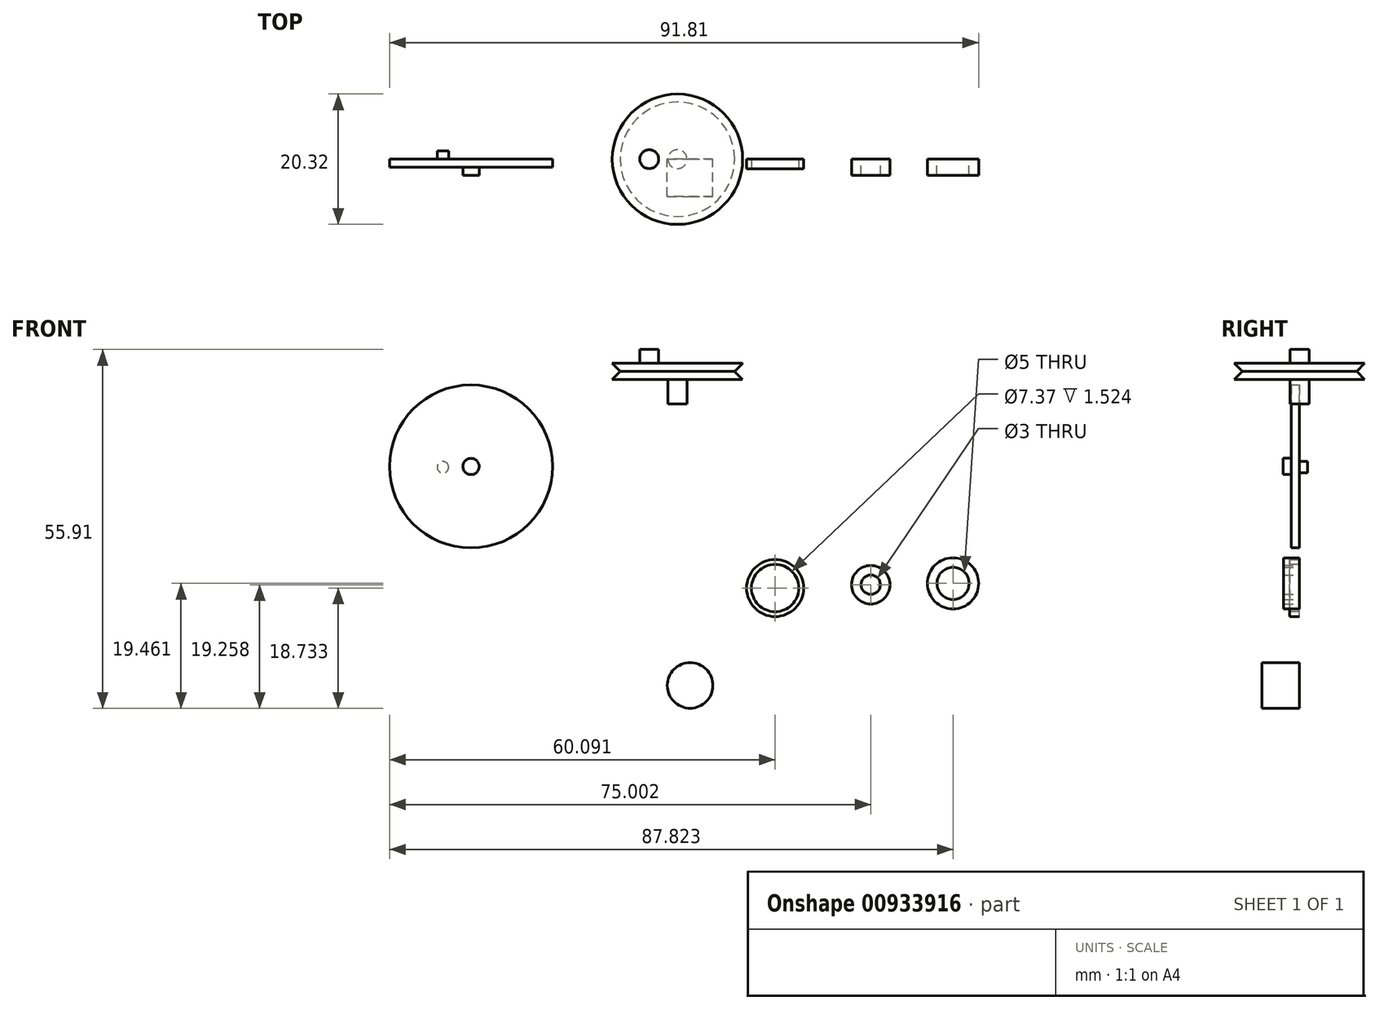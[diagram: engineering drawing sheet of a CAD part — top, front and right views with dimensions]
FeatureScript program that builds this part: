
annotation { "Feature Type Name" : "Feature", "Feature Type Description" : "" }
export const myFeature = defineFeature(function(context is Context, id is Id, definition is map)
    precondition{}
    {
        {
            var Q0;
            Q0=qCreatedBy(makeId("Front.planeOp"),FACE);
            var sketch = newSketch(context, id + "F0", { "sketchPlane" : qUnion([Q0])});
            skCircle(sketch, "E0", {"center": v(0, 0) * mm, "radius": 3.56 * mm});
            skSolve(sketch);
        }
        {
            var Q0;
            Q0=makeQuery(id+"F0.imprint","IMPRINT",FACE,{"disambiguationData":[TD([[makeQuery(id+"F0.imprint","IMPRINT",EDGE,{"derivedFrom":sQuery(id+"F0.wireOp",EDGE,"E0")}),1.0]])]});
            extrude(context, id + "F1", {"entities" : qUnion([Q0]), "depth" : 5.84 * mm, "offsetDistance" : 25.4 * mm});
        }
        {
            var Q0;
            Q0=qCreatedBy(makeId("Front.planeOp"),FACE);
            var sketch = newSketch(context, id + "F2", { "sketchPlane" : qUnion([Q0])});
            skCircle(sketch, "E1", {"center": v(13.25, 15.17) * mm, "radius": 4.45 * mm});
            skCircle(sketch, "E2", {"center": v(28.16, 15.7) * mm, "radius": 3 * mm});
            skCircle(sketch, "E3", {"center": v(40.98, 15.9) * mm, "radius": 3.99 * mm});
            skCircle(sketch, "E4", {"center": v(40.98, 15.9) * mm, "radius": 2.5 * mm});
            skCircle(sketch, "E5", {"center": v(28.16, 15.7) * mm, "radius": 1.5 * mm});
            skSolve(sketch);
        }
        {
            var Q0;
            Q0=makeQuery(id+"F2.imprint","IMPRINT",FACE,{"disambiguationData":[TD([[makeQuery(id+"F2.imprint","IMPRINT",EDGE,{"derivedFrom":sQuery(id+"F2.wireOp",EDGE,"E1")}),1.0]])]});
            extrude(context, id + "F3", {"entities" : qUnion([Q0]), "depth" : 1.52 * mm, "offsetDistance" : 25.4 * mm});
        }
        {
            var Q0;
            Q0=makeQuery(id+"F3.opExtrude","CAP_FACE",FACE,{"disambiguationData":[OSD([sQuery(id+"F2.wireOp",EDGE,"E1")])],"isStart":false});
            var sketch = newSketch(context, id + "F4", { "sketchPlane" : qUnion([Q0])});
            skCircle(sketch, "E6", {"center": v(13.25, 15.17) * mm, "radius": 3.68 * mm});
            skSolve(sketch);
        }
        {
            var Q0;
            Q0=makeQuery(id+"F4.imprint","IMPRINT",FACE,{"disambiguationData":[TD([[makeQuery(id+"F4.imprint","IMPRINT",EDGE,{"derivedFrom":sQuery(id+"F4.wireOp",EDGE,"E6")}),1.0]])]});
            extrude(context, id + "F5", {"entities" : qUnion([Q0]), "operationType" : NewBodyOperationType.REMOVE, "oppositeDirection" : true, "depth" : 25.4 * mm, "offsetDistance" : 25.4 * mm});
        }
        {
            var Q0;
            Q0=qCreatedBy(makeId("Front.planeOp"),FACE);
            var sketch = newSketch(context, id + "F6", { "sketchPlane" : qUnion([Q0])});
            skCircle(sketch, "E7", {"center": v(-34.14, 34.13) * mm, "radius": 12.7 * mm});
            skCircle(sketch, "E8", {"center": v(-34.14, 34.13) * mm, "radius": 1.27 * mm});
            skCircle(sketch, "E9", {"center": v(-38.52, 34) * mm, "radius": 0.89 * mm});
            skLineSegment(sketch, "E10.bottom", {"start": v(-12.13, 50.19) * mm, "end": v(-1.97, 50.19) * mm});
            skLineSegment(sketch, "E10.top", {"start": v(-12.13, 47.65) * mm, "end": v(-1.97, 47.65) * mm});
            skLineSegment(sketch, "E10.right", {"start": v(-1.97, 50.19) * mm, "end": v(-1.97, 47.65) * mm});
            skLineSegment(sketch, "E11", {"start": v(-10.89, 48.92) * mm, "end": v(-12.13, 50.19) * mm});
            skLineSegment(sketch, "E12", {"start": v(-10.89, 48.92) * mm, "end": v(-12.13, 47.65) * mm});
            skSolve(sketch);
        }
        {
            var Q0;
            Q0=makeQuery(id+"F6.imprint","IMPRINT",FACE,{"disambiguationData":[TD([[makeQuery(id+"F6.imprint","IMPRINT",EDGE,{"derivedFrom":sQuery(id+"F6.wireOp",EDGE,"E7")}),1.0]])]});
            var Q1;
            Q1=makeQuery(id+"F6.imprint","IMPRINT",FACE,{"disambiguationData":[TD([[makeQuery(id+"F6.imprint","IMPRINT",EDGE,{"derivedFrom":sQuery(id+"F6.wireOp",EDGE,"E9")}),1.0]])]});
            var Q2;
            Q2=makeQuery(id+"F6.imprint","IMPRINT",FACE,{"disambiguationData":[TD([[makeQuery(id+"F6.imprint","IMPRINT",EDGE,{"derivedFrom":sQuery(id+"F6.wireOp",EDGE,"E8")}),1.0]])]});
            extrude(context, id + "F7", {"entities" : qUnion([Q0, Q1, Q2]), "depth" : 1.27 * mm, "offsetDistance" : 25.4 * mm});
        }
        {
            var Q0;
            Q0=makeQuery(id+"F6.imprint","IMPRINT",FACE,{"disambiguationData":[TD([[makeQuery(id+"F6.imprint","IMPRINT",EDGE,{"derivedFrom":sQuery(id+"F6.wireOp",EDGE,"E9")}),1.0]])]});
            extrude(context, id + "F8", {"entities" : qUnion([Q0]), "operationType" : NewBodyOperationType.ADD, "oppositeDirection" : true, "depth" : 1.27 * mm, "offsetDistance" : 25.4 * mm});
        }
        {
            var Q0;
            Q0=makeQuery(id+"F6.imprint","IMPRINT",FACE,{"disambiguationData":[TD([[makeQuery(id+"F6.imprint","IMPRINT",EDGE,{"derivedFrom":sQuery(id+"F6.wireOp",EDGE,"E8")}),1.0]])]});
            extrude(context, id + "F9", {"entities" : qUnion([Q0]), "operationType" : NewBodyOperationType.ADD, "depth" : 2.54 * mm, "offsetDistance" : 25.4 * mm});
        }
        {
            var Q0;
            Q0=makeQuery(id+"F6.imprint","IMPRINT",FACE,{"disambiguationData":[TD([[makeQuery(id+"F6.imprint","IMPRINT",EDGE,{"derivedFrom":sQuery(id+"F6.wireOp",EDGE,"E10.bottom")}),-1.0]])]});
            var Q1;
            Q1=makeQuery(id+"F6.imprint","IMPRINT",FACE,{"disambiguationData":[TD([[makeQuery(id+"F6.imprint","IMPRINT",EDGE,{"derivedFrom":sQuery(id+"F6.wireOp",EDGE,"E10.right")}),1.0]])]});
            var Q2;
            Q2=sQuery(id+"F6.wireOp",EDGE,"E10.right");
            revolve(context, id + "F10", {"surfaceOperationType" : NewSurfaceOperationType.NEW, "entities" : qUnion([Q0, Q1]), "axis" : qUnion([Q2]), "revolveType" : RevolveType.FULL});
        }
        {
            var Q0;
            Q0=makeQuery(id+"F10.opRevolve","SWEPT_FACE",FACE,{"disambiguationData":[OSD([sQuery(id+"F6.wireOp",EDGE,"E10.bottom")])]});
            var sketch = newSketch(context, id + "F11", { "sketchPlane" : qUnion([Q0])});
            skLineSegment(sketch, "E13", {"start": v(-1.97, 0) * mm, "end": v(-6.37, 0) * mm});
            skCircle(sketch, "E14", {"center": v(-6.37, 0) * mm, "radius": 1.47 * mm});
            skSolve(sketch);
        }
        {
            var Q0;
            Q0=makeQuery(id+"F11.imprint","IMPRINT",FACE,{"disambiguationData":[TD([[makeQuery(id+"F11.imprint","IMPRINT",EDGE,{"derivedFrom":sQuery(id+"F11.wireOp",EDGE,"E14")}),1.0]])]});
            extrude(context, id + "F12", {"entities" : qUnion([Q0]), "operationType" : NewBodyOperationType.ADD, "depth" : 2.16 * mm, "offsetDistance" : 25.4 * mm});
        }
        {
            var Q0;
            Q0=makeQuery(id+"F2.imprint","IMPRINT",FACE,{"disambiguationData":[TD([[makeQuery(id+"F2.imprint","IMPRINT",EDGE,{"derivedFrom":sQuery(id+"F2.wireOp",EDGE,"E2")}),1.0]])]});
            var Q1;
            Q1=makeQuery(id+"F2.imprint","IMPRINT",FACE,{"disambiguationData":[TD([[makeQuery(id+"F2.imprint","IMPRINT",EDGE,{"derivedFrom":sQuery(id+"F2.wireOp",EDGE,"E3")}),1.0]])]});
            extrude(context, id + "F13", {"entities" : qUnion([Q0, Q1]), "depth" : 2.5 * mm, "offsetDistance" : 25.4 * mm});
        }
        {
            var Q0;
            Q0=makeQuery(id+"F10.opRevolve","SWEPT_FACE",FACE,{"disambiguationData":[OSD([sQuery(id+"F6.wireOp",EDGE,"E10.top")])]});
            var sketch = newSketch(context, id + "F14", { "sketchPlane" : qUnion([Q0])});
            skCircle(sketch, "E15", {"center": v(-1.97, 0) * mm, "radius": 1.47 * mm});
            skSolve(sketch);
        }
        {
            var Q0;
            Q0=makeQuery(id+"F14.imprint","IMPRINT",FACE,{"disambiguationData":[TD([[makeQuery(id+"F14.imprint","IMPRINT",EDGE,{"derivedFrom":sQuery(id+"F14.wireOp",EDGE,"E15")}),1.0]])]});
            extrude(context, id + "F15", {"entities" : qUnion([Q0]), "operationType" : NewBodyOperationType.ADD, "depth" : 3.8 * mm, "offsetDistance" : 25.4 * mm});
        }
    });
